# Revit family: SE_Trez_TC_300_With_Pit
name_source: partatom
category: Specialty Equipment
units: mm (PartAtom-declared; Revit-internal decimal feet)

## family parameters
Always vertical = Yes
Cut with Voids When Loaded = Yes
Maintain Annotation Orientation = No
Part Type = Normal
Room Calculation Point = No
Round Connector Dimension = Use Diameter
Shared = No
Work Plane-Based = No

## types (1)
- Platform-1300x1000mm with Door Height 2500mm
    A-Side = No
    B-Side = Yes
    C-Side = Yes
    Cabin = Speciality_Equipment_Trez_Cabin_Sgl_C : Cabin
    Cabin or Platform = Speciality_Equipment_Trez_Platform_Sgl_C : Platform
    Clear Depth = 1000 mm  [stored 3.28084 ft]
    Clear Width = 1300 mm  [stored 4.26509 ft]
    Clearance = 270 mm
    D-Side = Yes
    Default Elevation = 0 mm  [stored 0 ft]
    Description = As a hydraulic, goods-only lift with one cylinder, the TC is the low-price solution for lifting goods between the floors.
    Door Clear Height = 2500 mm  [stored 8.2021 ft]
    Door Clear Width = 1300 mm  [stored 4.26509 ft]
    Headroom = 3100 mm  [stored 10.1706 ft]
    Manufacturer = TREZ Ltd.
    Model = TC 300
    Pit Height = 120 mm  [stored 0.393701 ft]
    Platform = Speciality_Equipment_Trez_Platform_Sgl_C : Platform
    Platform Material = TREZ_Steel
    Profiles Material = TREZ_Steel
    Rail Height = 11580 mm
    Real Depth = 1000 mm  [stored 3.28084 ft]
    Real Width = 1300 mm  [stored 4.26509 ft]
    Safe Space = 600 mm
    Safe Working Load = 300.00 kg
    Shaft Depth = 1270 mm
    Shaft Width = 1400 mm
    Tower Cladding Material = TREZ_Steel_Cladding
    Travel = 8360 mm  [stored 27.4278 ft]
    URL = https://trez.bg

note: [stored X ft] marks values corroborated as IEEE doubles in the binary element streams (Revit-internal decimal feet)

## geometry (parser evidence)
native form markers: Sweep x10
no freeform markers — native parametric forms only
